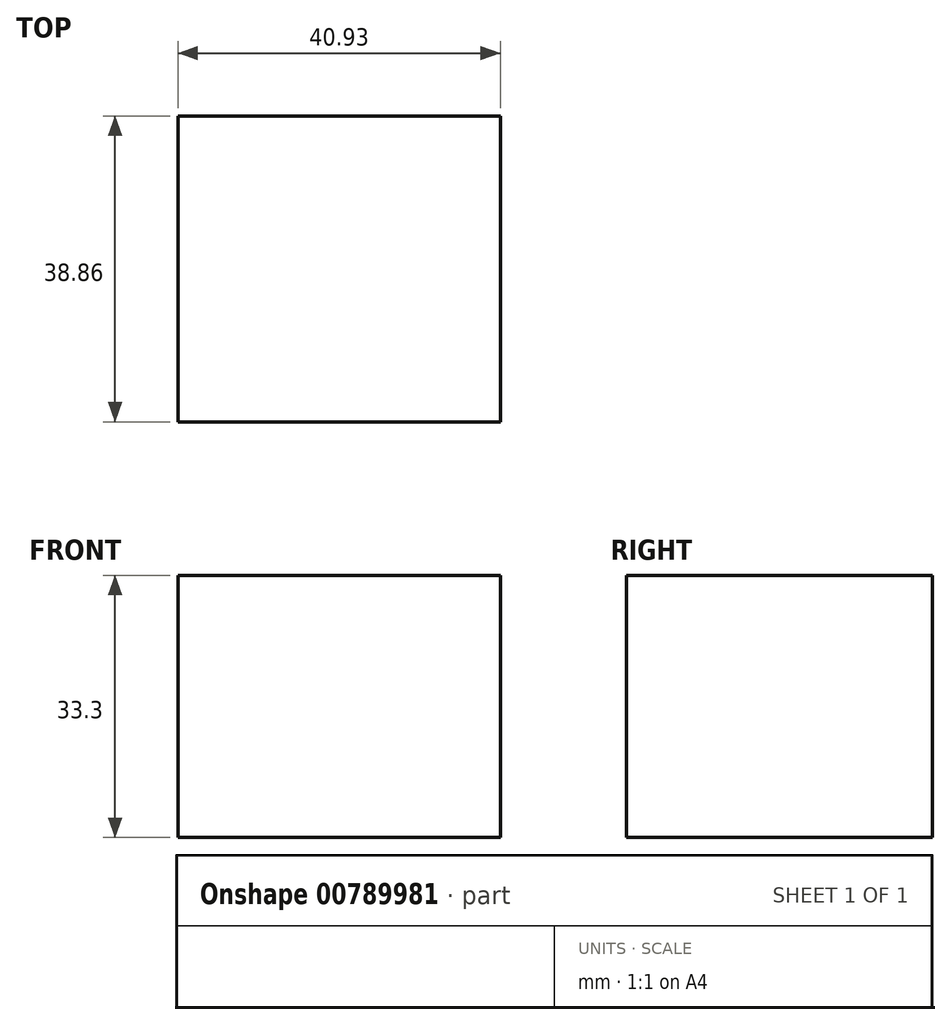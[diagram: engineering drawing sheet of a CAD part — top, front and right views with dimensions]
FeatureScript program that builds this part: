
annotation { "Feature Type Name" : "Feature", "Feature Type Description" : "" }
export const myFeature = defineFeature(function(context is Context, id is Id, definition is map)
    precondition{}
    {
        {
            var Q0;
            Q0=qCreatedBy(makeId("Front.planeOp"),FACE);
            var sketch = newSketch(context, id + "F0", { "sketchPlane" : qUnion([Q0])});
            skLineSegment(sketch, "E0", {"start": v(0, 0) * mm, "end": v(0, 25.66) * mm});
            skLineSegment(sketch, "E1", {"start": v(0, 25.66) * mm, "end": v(-14.6, 25.66) * mm});
            skLineSegment(sketch, "E2", {"start": v(-14.6, 25.66) * mm, "end": v(-14.6, 0) * mm});
            skLineSegment(sketch, "E3", {"start": v(-14.6, 0) * mm, "end": v(0, 0) * mm});
            skLineSegment(sketch, "E4", {"start": v(-14.6, 0) * mm, "end": v(-14.6, -7.64) * mm});
            skLineSegment(sketch, "E5", {"start": v(-14.6, -7.64) * mm, "end": v(26.34, -7.64) * mm});
            skLineSegment(sketch, "E6", {"start": v(26.34, -7.64) * mm, "end": v(26.34, 25.66) * mm});
            skLineSegment(sketch, "E7", {"start": v(26.34, 25.66) * mm, "end": v(0, 25.66) * mm});
            skLineSegment(sketch, "E8", {"start": v(7.15, 25.66) * mm, "end": v(26.34, 6.86) * mm});
            skSolve(sketch);
        }
        {
            var Q0;
            {var subQ3=sQuery(id+"F0.wireOp",EDGE,"E8");Q0=makeQuery(id+"F0.imprint","IMPRINT",FACE,{"disambiguationData":[TD([[makeQuery(id+"F0.imprint","IMPRINT",EDGE,{"derivedFrom":subQ3}),1.0]])]});}
            var Q1;
            {var subQ1=sQuery(id+"F0.wireOp",EDGE,"E0");Q1=makeQuery(id+"F0.imprint","IMPRINT",FACE,{"disambiguationData":[TD([[makeQuery(id+"F0.imprint","IMPRINT",EDGE,{"derivedFrom":subQ1}),-1.0]])]});}
            var Q2;
            Q2=makeQuery(id+"F0.imprint","IMPRINT",FACE,{"disambiguationData":[TD([[makeQuery(id+"F0.imprint","IMPRINT",EDGE,{"derivedFrom":sQuery(id+"F0.wireOp",EDGE,"E0")}),1.0]])]});
            extrude(context, id + "F1", {"entities" : qUnion([Q0, Q1, Q2]), "endBound" : BoundingType.SYMMETRIC, "depth" : 38.86 * mm, "offsetDistance" : 25.4 * mm});
        }
    });
